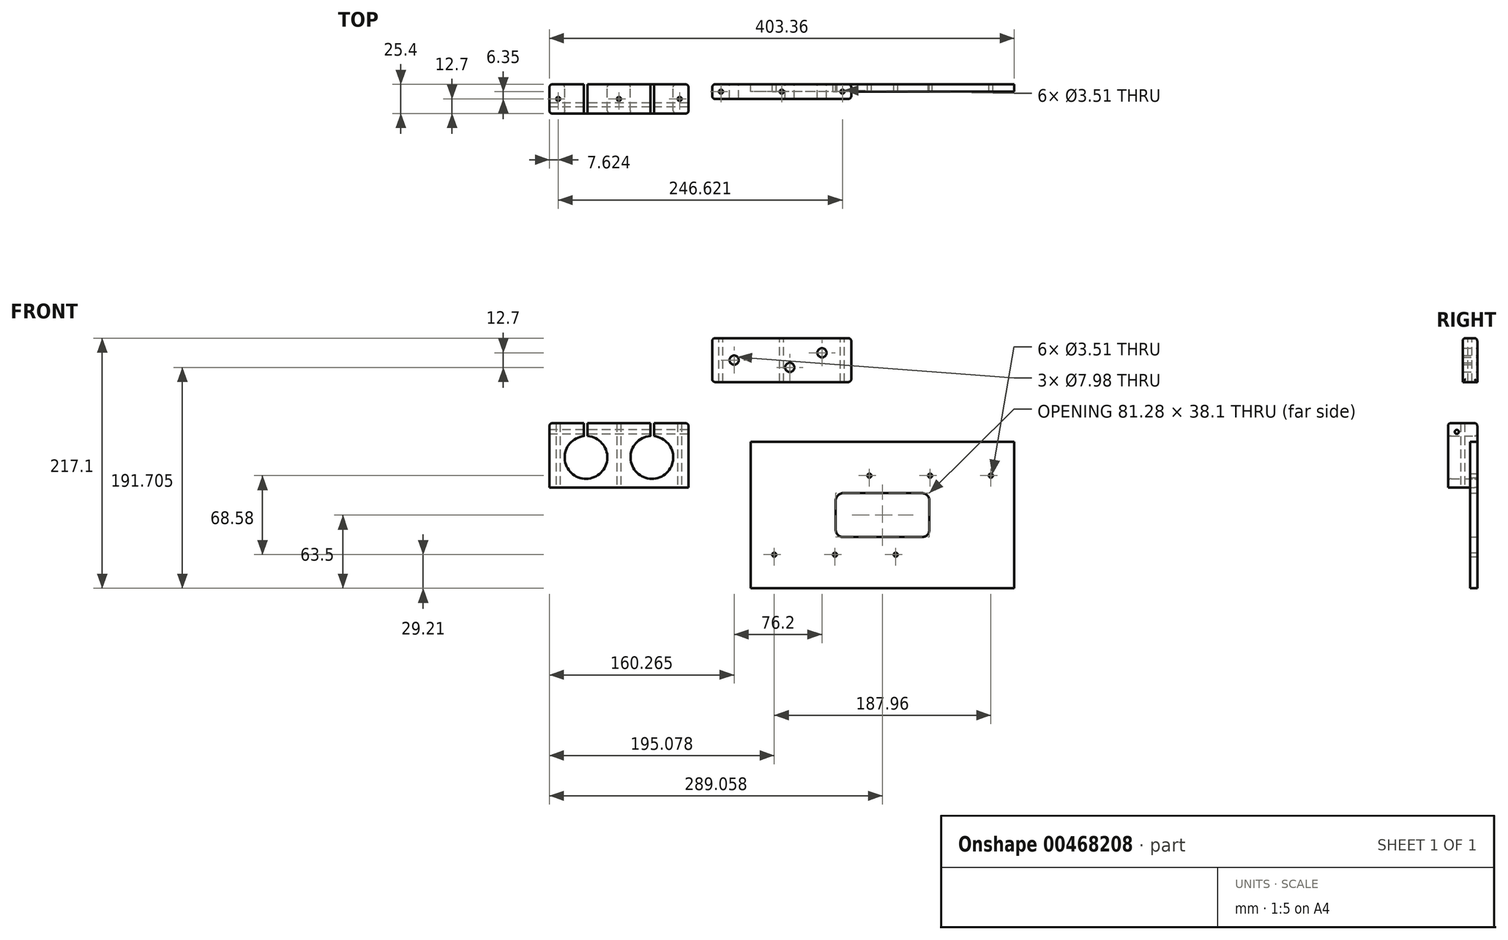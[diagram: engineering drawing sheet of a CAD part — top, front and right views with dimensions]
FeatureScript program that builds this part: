
annotation { "Feature Type Name" : "Feature", "Feature Type Description" : "" }
export const myFeature = defineFeature(function(context is Context, id is Id, definition is map)
    precondition{}
    {
        {
            var Q0;
            Q0=qCreatedBy(makeId("Front.planeOp"),FACE);
            var sketch = newSketch(context, id + "F0", { "sketchPlane" : qUnion([Q0])});
            skLineSegment(sketch, "E0.rect.bottom", {"start": v(60.33, -19.05) * mm, "end": v(-60.33, -19.05) * mm});
            skLineSegment(sketch, "E0.rect.top", {"start": v(47.63, 19.05) * mm, "end": v(-47.62, 19.05) * mm});
            skLineSegment(sketch, "E0.rect.left", {"start": v(60.33, -19.05) * mm, "end": v(60.33, 6.35) * mm});
            skLineSegment(sketch, "E0.rect.right", {"start": v(-60.33, -19.05) * mm, "end": v(-60.33, 6.35) * mm});
            skPoint(sketch, "E0.rect.middle", {"position": v(0, 0) * mm});
            skCircle(sketch, "E1", {"center": v(-41.28, 0) * mm, "radius": 3.99 * mm});
            skCircle(sketch, "E2", {"center": v(34.92, 6.35) * mm, "radius": 3.99 * mm});
            skCircle(sketch, "E3", {"center": v(6.98, -6.35) * mm, "radius": 3.99 * mm});
            skPoint(sketch, "E4.visualSharp", {"position": v(-60.33, 19.05) * mm});
            skPoint(sketch, "E5.visualSharp", {"position": v(60.33, 19.05) * mm});
            skLineSegment(sketch, "E6", {"start": v(-60.33, 6.35) * mm, "end": v(-60.33, 19.05) * mm});
            skLineSegment(sketch, "E7", {"start": v(-47.62, 19.05) * mm, "end": v(-60.33, 19.05) * mm});
            skLineSegment(sketch, "E8", {"start": v(60.33, 6.35) * mm, "end": v(60.33, 19.05) * mm});
            skLineSegment(sketch, "E9", {"start": v(47.63, 19.05) * mm, "end": v(60.33, 19.05) * mm});
            skSolve(sketch);
        }
        {
            var Q0;
            Q0=makeQuery(id+"F0.imprint","IMPRINT",FACE,{"disambiguationData":[TD([[makeQuery(id+"F0.imprint","IMPRINT",EDGE,{"derivedFrom":sQuery(id+"F0.wireOp",EDGE,"E0.rect.bottom")}),-1.0]])]});
            extrude(context, id + "F1", {"entities" : qUnion([Q0]), "depth" : 12.7 * mm});
        }
        {
            var Q0;
            Q0=makeQuery(id+"F1.opExtrude","SWEPT_FACE",FACE,{"disambiguationData":[OSD([sQuery(id+"F0.wireOp",EDGE,"E0.rect.top")])]});
            var sketch = newSketch(context, id + "F2", { "sketchPlane" : qUnion([Q0])});
            skLineSegment(sketch, "E10.0", {"start": v(-60.33, 0) * mm, "end": v(-60.33, -12.7) * mm});
            skLineSegment(sketch, "E10.3", {"start": v(60.33, -12.7) * mm, "end": v(60.33, 0) * mm});
            skLineSegment(sketch, "E10.4", {"start": v(47.63, -12.7) * mm, "end": v(-47.62, -12.7) * mm});
            skLineSegment(sketch, "E10.5", {"start": v(47.63, 0) * mm, "end": v(-47.62, 0) * mm});
            skPoint(sketch, "E11.centerSnap0", {"position": v(-47.62, -6.35) * mm});
            skCircle(sketch, "E12", {"center": v(52.7, -6.35) * mm, "radius": 1.75 * mm});
            skPoint(sketch, "E12.centerSnap0", {"position": v(47.63, -6.35) * mm});
            skCircle(sketch, "E13", {"center": v(0, -6.35) * mm, "radius": 1.75 * mm});
            skLineSegment(sketch, "E14", {"start": v(-47.62, -12.7) * mm, "end": v(-60.33, -12.7) * mm});
            skLineSegment(sketch, "E15", {"start": v(-60.33, 0) * mm, "end": v(-47.62, 0) * mm});
            skLineSegment(sketch, "E16", {"start": v(47.63, 0) * mm, "end": v(60.33, 0) * mm});
            skLineSegment(sketch, "E17", {"start": v(60.33, -12.7) * mm, "end": v(47.63, -12.7) * mm});
            skPoint(sketch, "E18", {"position": v(-60.33, -6.35) * mm});
            skCircle(sketch, "E19", {"center": v(-52.7, -6.35) * mm, "radius": 1.75 * mm});
            skSolve(sketch);
        }
        {
            var Q0;
            Q0=makeQuery(id+"F2.imprint","IMPRINT",FACE,{"disambiguationData":[TD([[makeQuery(id+"F2.imprint","IMPRINT",EDGE,{"derivedFrom":sQuery(id+"F2.wireOp",EDGE,"E12")}),1.0]])]});
            var Q1;
            Q1=makeQuery(id+"F2.imprint","IMPRINT",FACE,{"disambiguationData":[TD([[makeQuery(id+"F2.imprint","IMPRINT",EDGE,{"derivedFrom":sQuery(id+"F2.wireOp",EDGE,"E13")}),1.0]])]});
            var Q2;
            Q2=makeQuery(id+"F2.imprint","IMPRINT",FACE,{"disambiguationData":[TD([[makeQuery(id+"F2.imprint","IMPRINT",EDGE,{"derivedFrom":sQuery(id+"F2.wireOp",EDGE,"E19")}),1.0]])]});
            var Q3;
            Q3=makeQuery(id+"F1.opExtrude","SWEPT_FACE",FACE,{"disambiguationData":[OSD([sQuery(id+"F0.wireOp",EDGE,"E0.rect.bottom")])]});
            extrude(context, id + "F3", {"entities" : qUnion([Q0, Q1, Q2]), "operationType" : NewBodyOperationType.REMOVE, "endBound" : BoundingType.UP_TO_SURFACE, "oppositeDirection" : true, "endBoundEntityFace" : qUnion([Q3]), "depth" : 25.4 * mm});
        }
        {
            var Q0;
            Q0=makeQuery(id+"F1.opExtrude","CAP_EDGE",EDGE,{"disambiguationData":[OSD([sQuery(id+"F0.wireOp",EDGE,"E0.rect.top")])],"isStart":true});
            var Q1;
            Q1=makeQuery(id+"F1.opExtrude","CAP_EDGE",EDGE,{"disambiguationData":[OSD([sQuery(id+"F0.wireOp",EDGE,"E0.rect.top")])],"isStart":false});
            var Q2;
            Q2=makeQuery(id+"F1.opExtrude","CAP_EDGE",EDGE,{"disambiguationData":[OSD([sQuery(id+"F0.wireOp",EDGE,"E0.rect.right"),sQuery(id+"F0.wireOp",EDGE,"E6")])],"isStart":true});
            var Q3;
            Q3=makeQuery(id+"F1.opExtrude","CAP_EDGE",EDGE,{"disambiguationData":[OSD([sQuery(id+"F0.wireOp",EDGE,"E0.rect.left"),sQuery(id+"F0.wireOp",EDGE,"E8")])],"isStart":true});
            var Q4;
            Q4=makeQuery(id+"F1.opExtrude","CAP_EDGE",EDGE,{"disambiguationData":[OSD([sQuery(id+"F0.wireOp",EDGE,"E0.rect.left"),sQuery(id+"F0.wireOp",EDGE,"E8")])],"isStart":false});
            var Q5;
            Q5=makeQuery(id+"F1.opExtrude","CAP_EDGE",EDGE,{"disambiguationData":[OSD([sQuery(id+"F0.wireOp",EDGE,"E0.rect.right"),sQuery(id+"F0.wireOp",EDGE,"E6")])],"isStart":false});
            var Q6;
            Q6=makeQuery(id+"F1.opExtrude","SWEPT_FACE",FACE,{"disambiguationData":[OSD([sQuery(id+"F0.wireOp",EDGE,"E0.rect.left"),sQuery(id+"F0.wireOp",EDGE,"E8")])]});
            var Q7;
            Q7=makeQuery(id+"F1.opExtrude","SWEPT_FACE",FACE,{"disambiguationData":[OSD([sQuery(id+"F0.wireOp",EDGE,"E0.rect.right"),sQuery(id+"F0.wireOp",EDGE,"E6")])]});
            fillet(context, id + "F4", {"entities" : qUnion([Q0, Q1, Q2, Q3, Q4, Q5, Q6, Q7]), "radius" : 2.54 * mm, "tangentPropagation" : true, "allowEdgeOverflow" : false});
        }
        {
            var Q0;
            Q0=makeQuery(id+"F1.opExtrude","SWEPT_BODY",BODY,{"disambiguationData":[OSD([sQuery(id+"F0.wireOp",EDGE,"E0.rect.bottom"),sQuery(id+"F0.wireOp",EDGE,"E0.rect.top"),sQuery(id+"F0.wireOp",EDGE,"E0.rect.left"),sQuery(id+"F0.wireOp",EDGE,"E0.rect.right"),sQuery(id+"F0.wireOp",EDGE,"E1"),sQuery(id+"F0.wireOp",EDGE,"E2"),sQuery(id+"F0.wireOp",EDGE,"E3"),sQuery(id+"F0.wireOp",EDGE,"E4.filletArc"),sQuery(id+"F0.wireOp",EDGE,"E5.filletArc")])]});
            transform(context, id + "F5", {"entities" : qUnion([Q0]), "transformType" : TransformType.TRANSLATION_3D, "dx" : 61.2 * mm, "dy" : 0 * mm, "dz" : 45.02 * mm, "makeCopy" : false});
        }
        {
            var Q0;
            Q0=qCreatedBy(makeId("Front.planeOp"),FACE);
            var sketch = newSketch(context, id + "F6", { "sketchPlane" : qUnion([Q0])});
            skLineSegment(sketch, "E20.rect.bottom", {"start": v(-19.69, -65.58) * mm, "end": v(-140.34, -65.58) * mm});
            skLineSegment(sketch, "E20.rect.top", {"start": v(-19.69, -9.7) * mm, "end": v(-49.66, -9.7) * mm});
            skLineSegment(sketch, "E20.rect.left", {"start": v(-19.69, -65.58) * mm, "end": v(-19.69, -9.7) * mm});
            skLineSegment(sketch, "E20.rect.right", {"start": v(-140.34, -65.58) * mm, "end": v(-140.34, -9.7) * mm});
            skPoint(sketch, "E20.rect.middle", {"position": v(-80.01, -37.64) * mm});
            skArc(sketch, "E21", {"start": v(-110.36, -20.96) * mm, "mid": v(-108.4, -57.96) * mm, "end": v(-107.19, -20.92) * mm});
            skArc(sketch, "E22", {"start": v(-52.83, -20.92) * mm, "mid": v(-51.63, -57.96) * mm, "end": v(-49.66, -20.96) * mm});
            skLineSegment(sketch, "E23", {"start": v(-110.36, -20.96) * mm, "end": v(-110.36, -9.7) * mm});
            skLineSegment(sketch, "E24", {"start": v(-107.19, -20.92) * mm, "end": v(-107.19, -9.7) * mm});
            skLineSegment(sketch, "E25", {"start": v(-52.83, -20.92) * mm, "end": v(-52.83, -9.7) * mm});
            skLineSegment(sketch, "E26", {"start": v(-49.66, -20.96) * mm, "end": v(-49.66, -9.7) * mm});
            skLineSegment(sketch, "E27.trimOffspring", {"start": v(-110.36, -9.7) * mm, "end": v(-140.34, -9.7) * mm});
            skLineSegment(sketch, "E28.trimOffspring", {"start": v(-52.83, -9.7) * mm, "end": v(-107.19, -9.7) * mm});
            skSolve(sketch);
        }
        {
            var Q0;
            Q0=makeQuery(id+"F6.imprint","IMPRINT",FACE,{"disambiguationData":[TD([[makeQuery(id+"F6.imprint","IMPRINT",EDGE,{"derivedFrom":sQuery(id+"F6.wireOp",EDGE,"E20.rect.bottom")}),-1.0]])]});
            extrude(context, id + "F7", {"entities" : qUnion([Q0]), "depth" : 25.4 * mm});
        }
        {
            var Q0;
            Q0=makeQuery(id+"F7.opExtrude","SWEPT_FACE",FACE,{"disambiguationData":[OSD([sQuery(id+"F6.wireOp",EDGE,"E20.rect.right")])]});
            var sketch = newSketch(context, id + "F8", { "sketchPlane" : qUnion([Q0])});
            skCircle(sketch, "E29", {"center": v(17.78, -17.32) * mm, "radius": 1.75 * mm});
            skSolve(sketch);
        }
        {
            var Q0;
            Q0=makeQuery(id+"F8.imprint","IMPRINT",FACE,{"disambiguationData":[TD([[makeQuery(id+"F8.imprint","IMPRINT",EDGE,{"derivedFrom":sQuery(id+"F8.wireOp",EDGE,"E29")}),1.0]])]});
            extrude(context, id + "F9", {"entities" : qUnion([Q0]), "operationType" : NewBodyOperationType.REMOVE, "endBound" : BoundingType.THROUGH_ALL, "oppositeDirection" : true, "depth" : 25.4 * mm});
        }
        {
            var Q0;
            Q0=makeQuery(id+"F7.opExtrude","SWEPT_FACE",FACE,{"disambiguationData":[OSD([sQuery(id+"F6.wireOp",EDGE,"E20.rect.bottom")])]});
            var sketch = newSketch(context, id + "F10", { "sketchPlane" : qUnion([Q0])});
            skCircle(sketch, "E30", {"center": v(-132.72, 12.7) * mm, "radius": 1.75 * mm});
            skCircle(sketch, "E31", {"center": v(-80.01, 12.7) * mm, "radius": 1.75 * mm});
            skCircle(sketch, "E32", {"center": v(-27.3, 12.7) * mm, "radius": 1.75 * mm});
            skSolve(sketch);
        }
        {
            var Q0;
            Q0=makeQuery(id+"F10.imprint","IMPRINT",FACE,{"disambiguationData":[TD([[makeQuery(id+"F10.imprint","IMPRINT",EDGE,{"derivedFrom":sQuery(id+"F10.wireOp",EDGE,"E30")}),1.0]])]});
            var Q1;
            Q1=makeQuery(id+"F10.imprint","IMPRINT",FACE,{"disambiguationData":[TD([[makeQuery(id+"F10.imprint","IMPRINT",EDGE,{"derivedFrom":sQuery(id+"F10.wireOp",EDGE,"E31")}),1.0]])]});
            var Q2;
            Q2=makeQuery(id+"F10.imprint","IMPRINT",FACE,{"disambiguationData":[TD([[makeQuery(id+"F10.imprint","IMPRINT",EDGE,{"derivedFrom":sQuery(id+"F10.wireOp",EDGE,"E32")}),1.0]])]});
            extrude(context, id + "F11", {"entities" : qUnion([Q0, Q1, Q2]), "operationType" : NewBodyOperationType.REMOVE, "endBound" : BoundingType.THROUGH_ALL, "oppositeDirection" : true, "depth" : 25.4 * mm});
        }
        {
            var Q0;
            Q0=makeQuery(id+"F7.opExtrude","CAP_EDGE",EDGE,{"disambiguationData":[OSD([sQuery(id+"F6.wireOp",EDGE,"E20.rect.top")])],"isStart":false});
            var Q1;
            Q1=makeQuery(id+"F7.opExtrude","CAP_EDGE",EDGE,{"disambiguationData":[OSD([sQuery(id+"F6.wireOp",EDGE,"E28.trimOffspring")])],"isStart":false});
            var Q2;
            Q2=makeQuery(id+"F7.opExtrude","CAP_EDGE",EDGE,{"disambiguationData":[OSD([sQuery(id+"F6.wireOp",EDGE,"E27.trimOffspring")])],"isStart":false});
            var Q3;
            Q3=makeQuery(id+"F7.opExtrude","CAP_EDGE",EDGE,{"disambiguationData":[OSD([sQuery(id+"F6.wireOp",EDGE,"E20.rect.left")])],"isStart":false});
            var Q4;
            Q4=makeQuery(id+"F7.opExtrude","CAP_EDGE",EDGE,{"disambiguationData":[OSD([sQuery(id+"F6.wireOp",EDGE,"E20.rect.right")])],"isStart":false});
            var Q5;
            Q5=makeQuery(id+"F7.opExtrude","CAP_EDGE",EDGE,{"disambiguationData":[OSD([sQuery(id+"F6.wireOp",EDGE,"E20.rect.right")])],"isStart":true});
            var Q6;
            Q6=makeQuery(id+"F7.opExtrude","CAP_EDGE",EDGE,{"disambiguationData":[OSD([sQuery(id+"F6.wireOp",EDGE,"E27.trimOffspring")])],"isStart":true});
            var Q7;
            Q7=makeQuery(id+"F7.opExtrude","CAP_EDGE",EDGE,{"disambiguationData":[OSD([sQuery(id+"F6.wireOp",EDGE,"E28.trimOffspring")])],"isStart":true});
            var Q8;
            Q8=makeQuery(id+"F7.opExtrude","CAP_EDGE",EDGE,{"disambiguationData":[OSD([sQuery(id+"F6.wireOp",EDGE,"E20.rect.top")])],"isStart":true});
            var Q9;
            Q9=makeQuery(id+"F7.opExtrude","CAP_EDGE",EDGE,{"disambiguationData":[OSD([sQuery(id+"F6.wireOp",EDGE,"E20.rect.left")])],"isStart":true});
            var Q10;
            Q10=makeQuery(id+"F7.opExtrude","SWEPT_EDGE",EDGE,{"disambiguationData":[OSD([sQuery(id+"F6.wireOp",EDGE,"E20.rect.right"),sQuery(id+"F6.wireOp",EDGE,"E27.trimOffspring")])]});
            var Q11;
            Q11=makeQuery(id+"F7.opExtrude","SWEPT_EDGE",EDGE,{"disambiguationData":[OSD([sQuery(id+"F6.wireOp",EDGE,"E20.rect.top"),sQuery(id+"F6.wireOp",EDGE,"E20.rect.left")])]});
            var Q12;
            Q12=makeQuery(id+"F7.opExtrude","CAP_EDGE",EDGE,{"disambiguationData":[OSD([sQuery(id+"F6.wireOp",EDGE,"E21")])],"isStart":false});
            var Q13;
            Q13=makeQuery(id+"F7.opExtrude","CAP_EDGE",EDGE,{"disambiguationData":[OSD([sQuery(id+"F6.wireOp",EDGE,"E22")])],"isStart":false});
            var Q14;
            Q14=makeQuery(id+"F7.opExtrude","CAP_EDGE",EDGE,{"disambiguationData":[OSD([sQuery(id+"F6.wireOp",EDGE,"E22")])],"isStart":true});
            var Q15;
            Q15=makeQuery(id+"F7.opExtrude","CAP_EDGE",EDGE,{"disambiguationData":[OSD([sQuery(id+"F6.wireOp",EDGE,"E21")])],"isStart":true});
            fillet(context, id + "F12", {"entities" : qUnion([Q0, Q1, Q2, Q3, Q4, Q5, Q6, Q7, Q8, Q9, Q10, Q11, Q12, Q13, Q14, Q15]), "radius" : 2.54 * mm, "tangentPropagation" : true, "allowEdgeOverflow" : false});
        }
        {
            var Q0;
            Q0=qCreatedBy(makeId("Front.planeOp"),FACE);
            var sketch = newSketch(context, id + "F13", { "sketchPlane" : qUnion([Q0])});
            skLineSegment(sketch, "E33.bottom", {"start": v(263.02, -26.03) * mm, "end": v(34.42, -26.03) * mm});
            skLineSegment(sketch, "E33.top", {"start": v(263.02, -153.03) * mm, "end": v(34.42, -153.03) * mm});
            skLineSegment(sketch, "E33.left", {"start": v(263.02, -26.03) * mm, "end": v(263.02, -153.03) * mm});
            skLineSegment(sketch, "E33.right", {"start": v(34.42, -26.03) * mm, "end": v(34.42, -153.03) * mm});
            skLineSegment(sketch, "E34.bottom", {"start": v(183, -70.48) * mm, "end": v(114.43, -70.48) * mm});
            skLineSegment(sketch, "E34.top", {"start": v(183, -108.58) * mm, "end": v(114.43, -108.58) * mm});
            skLineSegment(sketch, "E34.left", {"start": v(189.36, -76.83) * mm, "end": v(189.36, -102.23) * mm});
            skLineSegment(sketch, "E34.right", {"start": v(108.08, -76.83) * mm, "end": v(108.08, -102.23) * mm});
            skPoint(sketch, "E35.visualSharp", {"position": v(189.36, -70.48) * mm});
            skArc(sketch, "E35.filletArc", {"start": v(189.36, -76.83) * mm, "mid": v(187.5, -72.34) * mm, "end": v(183, -70.48) * mm});
            skPoint(sketch, "E36.visualSharp", {"position": v(108.08, -70.48) * mm});
            skArc(sketch, "E36.filletArc", {"start": v(114.43, -70.48) * mm, "mid": v(109.94, -72.34) * mm, "end": v(108.08, -76.83) * mm});
            skPoint(sketch, "E37.visualSharp", {"position": v(108.08, -108.58) * mm});
            skArc(sketch, "E37.filletArc", {"start": v(108.08, -102.23) * mm, "mid": v(109.94, -106.72) * mm, "end": v(114.43, -108.58) * mm});
            skPoint(sketch, "E38.visualSharp", {"position": v(189.36, -108.58) * mm});
            skArc(sketch, "E38.filletArc", {"start": v(183, -108.58) * mm, "mid": v(187.5, -106.72) * mm, "end": v(189.36, -102.23) * mm});
            skLineSegment(sketch, "E39.bottom", {"start": v(250.32, -48.89) * mm, "end": v(129.67, -48.89) * mm});
            skLineSegment(sketch, "E39.top", {"start": v(250.32, -61.59) * mm, "end": v(129.67, -61.59) * mm});
            skLineSegment(sketch, "E39.left", {"start": v(250.32, -48.89) * mm, "end": v(250.32, -61.59) * mm});
            skLineSegment(sketch, "E39.right", {"start": v(129.67, -48.89) * mm, "end": v(129.67, -61.59) * mm});
            skLineSegment(sketch, "E40.bottom", {"start": v(167.77, -117.47) * mm, "end": v(47.12, -117.47) * mm});
            skLineSegment(sketch, "E40.top", {"start": v(167.77, -130.17) * mm, "end": v(47.12, -130.17) * mm});
            skLineSegment(sketch, "E40.left", {"start": v(167.77, -117.47) * mm, "end": v(167.77, -130.17) * mm});
            skLineSegment(sketch, "E40.right", {"start": v(47.12, -117.47) * mm, "end": v(47.12, -130.17) * mm});
            skCircle(sketch, "E41", {"center": v(242.7, -55.24) * mm, "radius": 1.75 * mm});
            skPoint(sketch, "E41.centerSnap0", {"position": v(250.32, -55.24) * mm});
            skCircle(sketch, "E42", {"center": v(137.29, -55.24) * mm, "radius": 1.75 * mm});
            skPoint(sketch, "E42.centerSnap0", {"position": v(129.67, -55.24) * mm});
            skCircle(sketch, "E43", {"center": v(54.74, -123.82) * mm, "radius": 1.75 * mm});
            skPoint(sketch, "E43.centerSnap0", {"position": v(47.12, -123.82) * mm});
            skCircle(sketch, "E44", {"center": v(160.15, -123.82) * mm, "radius": 1.75 * mm});
            skPoint(sketch, "E44.centerSnap0", {"position": v(167.77, -123.82) * mm});
            skCircle(sketch, "E45", {"center": v(190, -55.24) * mm, "radius": 1.75 * mm});
            skCircle(sketch, "E46", {"center": v(107.44, -123.82) * mm, "radius": 1.75 * mm});
            skSolve(sketch);
        }
        {
            var Q0;
            Q0=makeQuery(id+"F13.imprint","IMPRINT",FACE,{"disambiguationData":[TD([[makeQuery(id+"F13.imprint","IMPRINT",EDGE,{"derivedFrom":sQuery(id+"F13.wireOp",EDGE,"E33.bottom")}),1.0]])]});
            var Q1;
            Q1=makeQuery(id+"F13.imprint","IMPRINT",FACE,{"disambiguationData":[TD([[makeQuery(id+"F13.imprint","IMPRINT",EDGE,{"derivedFrom":sQuery(id+"F13.wireOp",EDGE,"E39.bottom")}),1.0]])]});
            var Q2;
            Q2=makeQuery(id+"F13.imprint","IMPRINT",FACE,{"disambiguationData":[TD([[makeQuery(id+"F13.imprint","IMPRINT",EDGE,{"derivedFrom":sQuery(id+"F13.wireOp",EDGE,"E40.bottom")}),1.0]])]});
            extrude(context, id + "F14", {"entities" : qUnion([Q0, Q1, Q2]), "depth" : 6.35 * mm});
        }
        {
            var Q0;
            Q0=makeQuery(id+"F1.opExtrude","SWEPT_BODY",BODY,{"disambiguationData":[OSD([sQuery(id+"F0.wireOp",EDGE,"E0.rect.bottom"),sQuery(id+"F0.wireOp",EDGE,"E0.rect.top"),sQuery(id+"F0.wireOp",EDGE,"E0.rect.left"),sQuery(id+"F0.wireOp",EDGE,"E0.rect.right"),sQuery(id+"F0.wireOp",EDGE,"E1"),sQuery(id+"F0.wireOp",EDGE,"E2"),sQuery(id+"F0.wireOp",EDGE,"E3"),sQuery(id+"F0.wireOp",EDGE,"E4.filletArc"),sQuery(id+"F0.wireOp",EDGE,"E5.filletArc")])]});
            transform(context, id + "F15", {"entities" : qUnion([Q0]), "transformType" : TransformType.TRANSLATION_3D, "dx" : -142.4 * mm, "dy" : 0 * mm, "dz" : 0 * mm, "makeCopy" : true});
        }
        {
            var Q0;
            Q0=makeQuery(id+"F15.opPattern","COPY",BODY,{"derivedFrom":makeQuery(id+"F1.opExtrude","SWEPT_BODY",BODY,{"disambiguationData":[OSD([sQuery(id+"F0.wireOp",EDGE,"E0.rect.bottom"),sQuery(id+"F0.wireOp",EDGE,"E0.rect.top"),sQuery(id+"F0.wireOp",EDGE,"E0.rect.left"),sQuery(id+"F0.wireOp",EDGE,"E0.rect.right"),sQuery(id+"F0.wireOp",EDGE,"E1"),sQuery(id+"F0.wireOp",EDGE,"E2"),sQuery(id+"F0.wireOp",EDGE,"E3"),sQuery(id+"F0.wireOp",EDGE,"E4.filletArc"),sQuery(id+"F0.wireOp",EDGE,"E5.filletArc")])]}),"instanceName":"1"});
            deleteBodies(context, id + "F16", {"entities" : qUnion([Q0])});
        }
    });
